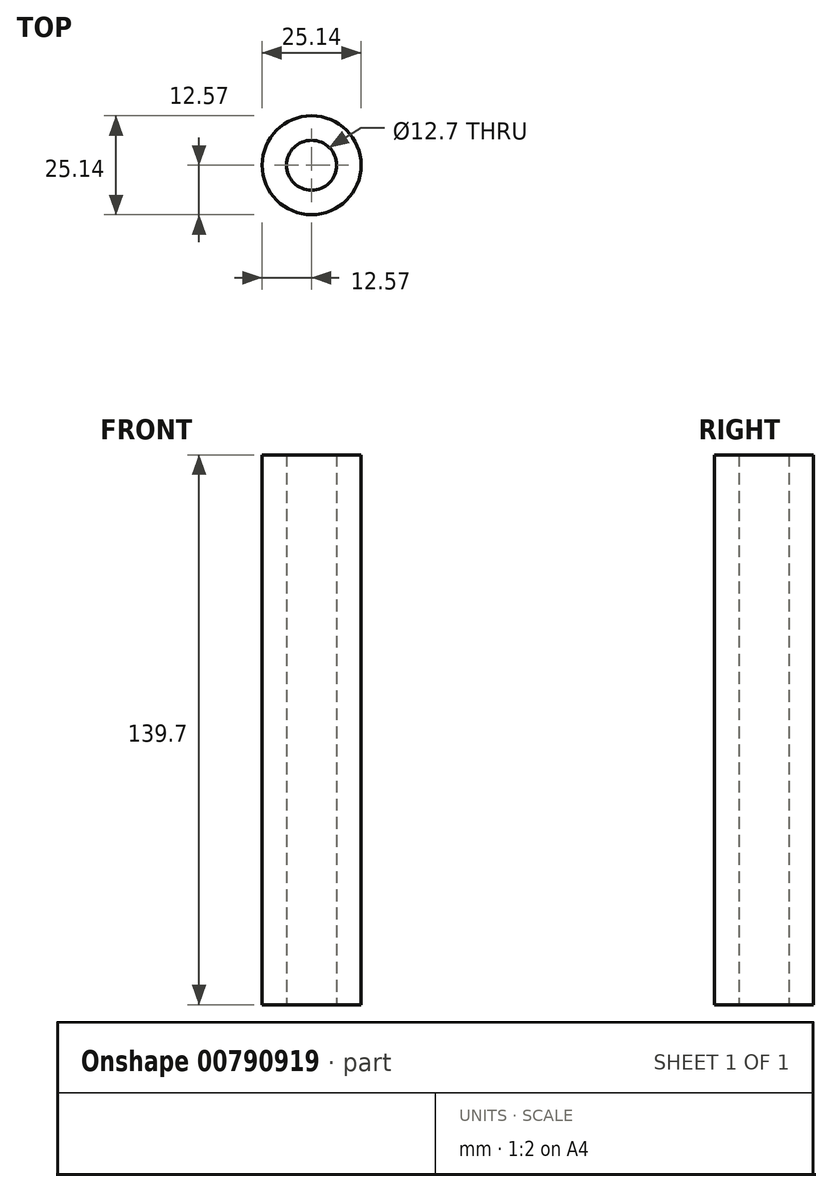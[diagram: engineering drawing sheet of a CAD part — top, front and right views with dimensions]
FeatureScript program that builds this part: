
annotation { "Feature Type Name" : "Feature", "Feature Type Description" : "" }
export const myFeature = defineFeature(function(context is Context, id is Id, definition is map)
    precondition{}
    {
        {
            var Q0;
            Q0=qCreatedBy(makeId("Top.planeOp"),FACE);
            var sketch = newSketch(context, id + "F0", { "sketchPlane" : qUnion([Q0])});
            skCircle(sketch, "E0", {"center": v(0, 0) * mm, "radius": 6.35 * mm});
            skCircle(sketch, "E1", {"center": v(0, 0) * mm, "radius": 12.57 * mm});
            skSolve(sketch);
        }
        {
            var Q0;
            Q0 = qSketchRegion(id + "F0", true);
            extrude(context, id + "F1", {"entities" : qUnion([Q0]), "depth" : 139.7 * mm, "offsetDistance" : 25.4 * mm});
        }
    });
